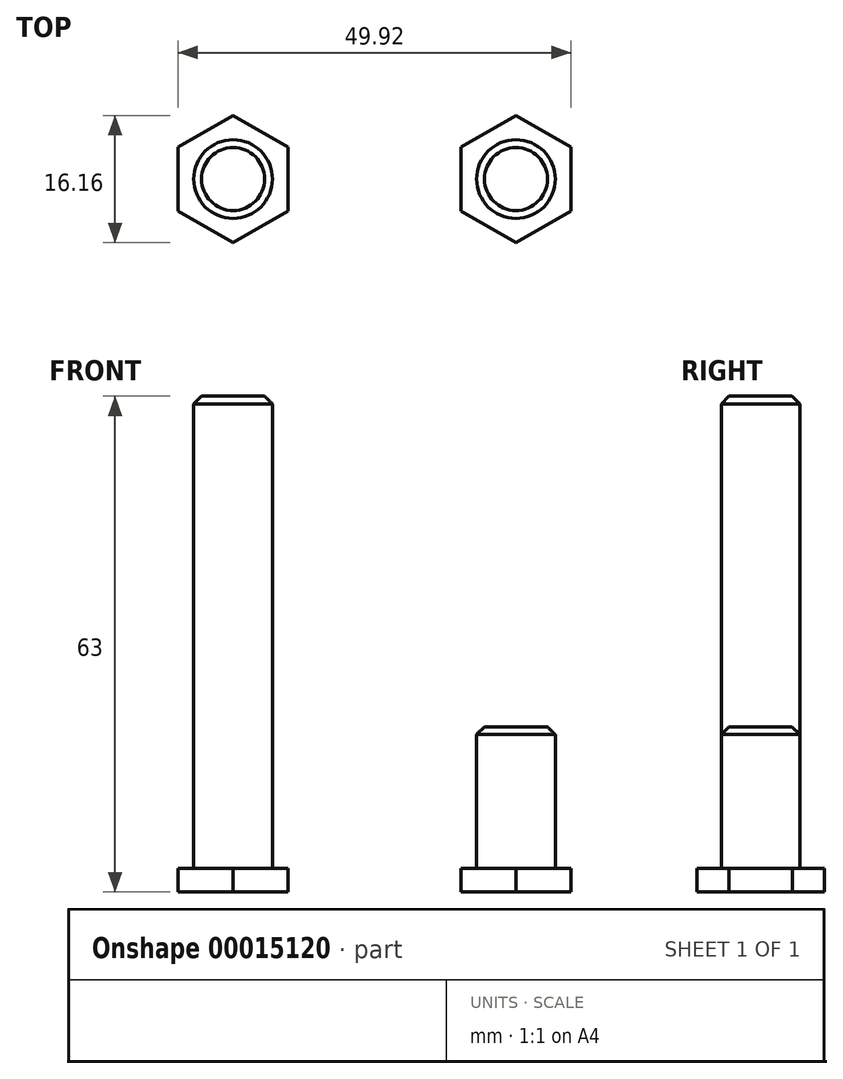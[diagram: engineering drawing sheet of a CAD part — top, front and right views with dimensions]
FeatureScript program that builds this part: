
annotation { "Feature Type Name" : "Feature", "Feature Type Description" : "" }
export const myFeature = defineFeature(function(context is Context, id is Id, definition is map)
    precondition{}
    {
        {
            var Q0;
            Q0=qCreatedBy(makeId("Top.planeOp"),FACE);
            var sketch = newSketch(context, id + "F0", { "sketchPlane" : qUnion([Q0])});
            skCircle(sketch, "E0.cCircle", {"center": v(17.96, 0) * mm, "radius": 7 * mm, "construction": true});
            skLineSegment(sketch, "E0.0", {"start": v(24.96, -4.04) * mm, "end": v(17.96, -8.08) * mm});
            skLineSegment(sketch, "E0.1", {"start": v(17.96, -8.08) * mm, "end": v(10.96, -4.04) * mm});
            skLineSegment(sketch, "E0.2", {"start": v(10.96, -4.04) * mm, "end": v(10.96, 4.04) * mm});
            skLineSegment(sketch, "E0.3", {"start": v(10.96, 4.04) * mm, "end": v(17.96, 8.08) * mm});
            skLineSegment(sketch, "E0.4", {"start": v(17.96, 8.08) * mm, "end": v(24.96, 4.04) * mm});
            skLineSegment(sketch, "E0.5", {"start": v(24.96, 4.04) * mm, "end": v(24.96, -4.04) * mm});
            skPoint(sketch, "E0.0.midPoint", {"position": v(21.46, -6.06) * mm});
            skLineSegment(sketch, "E1", {"start": v(0, 0) * mm, "end": v(0, 16.6) * mm, "construction": true});
            skLineSegment(sketch, "E2.0.MirrorCS", {"start": v(-10.96, -4.04) * mm, "end": v(-10.96, 4.04) * mm});
            skLineSegment(sketch, "E3.0.MirrorCS", {"start": v(-10.96, 4.04) * mm, "end": v(-17.96, 8.08) * mm});
            skLineSegment(sketch, "E4.0.MirrorCS", {"start": v(-17.96, 8.08) * mm, "end": v(-24.96, 4.04) * mm});
            skLineSegment(sketch, "E5.0.MirrorCS", {"start": v(-24.96, 4.04) * mm, "end": v(-24.96, -4.04) * mm});
            skPoint(sketch, "E6.0.MirrorP", {"position": v(-21.46, -6.06) * mm});
            skLineSegment(sketch, "E7.0.MirrorCS", {"start": v(-17.96, -8.08) * mm, "end": v(-10.96, -4.04) * mm});
            skLineSegment(sketch, "E8.0.MirrorCS", {"start": v(-24.96, -4.04) * mm, "end": v(-17.96, -8.08) * mm});
            skSolve(sketch);
        }
        {
            var Q0;
            Q0=makeQuery(id+"F0.imprint","IMPRINT",FACE,{"disambiguationData":[TD([[makeQuery(id+"F0.imprint","IMPRINT",EDGE,{"derivedFrom":sQuery(id+"F0.wireOp",EDGE,"E2.0.MirrorCS")}),1.0]])]});
            var Q1;
            Q1=makeQuery(id+"F0.imprint","IMPRINT",FACE,{"disambiguationData":[TD([[makeQuery(id+"F0.imprint","IMPRINT",EDGE,{"derivedFrom":sQuery(id+"F0.wireOp",EDGE,"E0.0")}),-1.0]])]});
            extrude(context, id + "F1", {"entities" : qUnion([Q0, Q1]), "depth" : 3 * mm});
        }
        {
            var Q0;
            Q0=makeQuery(id+"F1.opExtrude","CAP_FACE",FACE,{"disambiguationData":[OSD([sQuery(id+"F0.wireOp",EDGE,"E2.0.MirrorCS"),sQuery(id+"F0.wireOp",EDGE,"E3.0.MirrorCS"),sQuery(id+"F0.wireOp",EDGE,"E4.0.MirrorCS"),sQuery(id+"F0.wireOp",EDGE,"E5.0.MirrorCS"),sQuery(id+"F0.wireOp",EDGE,"E7.0.MirrorCS"),sQuery(id+"F0.wireOp",EDGE,"E8.0.MirrorCS")])],"isStart":false});
            var sketch = newSketch(context, id + "F2", { "sketchPlane" : qUnion([Q0])});
            skLineSegment(sketch, "E9.0.0", {"start": v(-17.96, -8.08) * mm, "end": v(-10.96, -4.04) * mm});
            skLineSegment(sketch, "E9.0.1", {"start": v(-10.96, -4.04) * mm, "end": v(-10.96, 4.04) * mm});
            skLineSegment(sketch, "E9.0.2", {"start": v(-10.96, 4.04) * mm, "end": v(-17.96, 8.08) * mm});
            skLineSegment(sketch, "E9.0.3", {"start": v(-17.96, 8.08) * mm, "end": v(-24.96, 4.04) * mm});
            skLineSegment(sketch, "E9.0.4", {"start": v(-24.96, 4.04) * mm, "end": v(-24.96, -4.04) * mm});
            skLineSegment(sketch, "E9.0.5", {"start": v(-24.96, -4.04) * mm, "end": v(-17.96, -8.08) * mm});
            skLineSegment(sketch, "E10.0.0", {"start": v(17.96, -8.08) * mm, "end": v(24.96, -4.04) * mm});
            skLineSegment(sketch, "E10.0.1", {"start": v(24.96, -4.04) * mm, "end": v(24.96, 4.04) * mm});
            skLineSegment(sketch, "E10.0.2", {"start": v(24.96, 4.04) * mm, "end": v(17.96, 8.08) * mm});
            skLineSegment(sketch, "E10.0.3", {"start": v(17.96, 8.08) * mm, "end": v(10.96, 4.04) * mm});
            skLineSegment(sketch, "E10.0.4", {"start": v(10.96, 4.04) * mm, "end": v(10.96, -4.04) * mm});
            skLineSegment(sketch, "E10.0.5", {"start": v(10.96, -4.04) * mm, "end": v(17.96, -8.08) * mm});
            skLineSegment(sketch, "E11", {"start": v(-17.96, 8.08) * mm, "end": v(-17.96, -8.08) * mm, "construction": true});
            skLineSegment(sketch, "E12", {"start": v(-24.96, 4.04) * mm, "end": v(-10.96, -4.04) * mm, "construction": true});
            skLineSegment(sketch, "E13", {"start": v(10.96, 4.04) * mm, "end": v(24.96, -4.04) * mm, "construction": true});
            skLineSegment(sketch, "E14", {"start": v(17.96, 8.08) * mm, "end": v(17.96, -8.08) * mm, "construction": true});
            skCircle(sketch, "E15", {"center": v(-17.96, 0) * mm, "radius": 5 * mm});
            skCircle(sketch, "E16", {"center": v(17.96, 0) * mm, "radius": 5 * mm});
            skSolve(sketch);
        }
        {
            var Q0;
            Q0=makeQuery(id+"F2.imprint","IMPRINT",FACE,{"disambiguationData":[TD([[makeQuery(id+"F2.imprint","IMPRINT",EDGE,{"derivedFrom":sQuery(id+"F2.wireOp",EDGE,"E16")}),1.0]])]});
            extrude(context, id + "F3", {"entities" : qUnion([Q0]), "operationType" : NewBodyOperationType.ADD, "depth" : 18 * mm});
        }
        {
            var Q0;
            Q0=makeQuery(id+"F2.imprint","IMPRINT",FACE,{"disambiguationData":[TD([[makeQuery(id+"F2.imprint","IMPRINT",EDGE,{"derivedFrom":sQuery(id+"F2.wireOp",EDGE,"E15")}),1.0]])]});
            extrude(context, id + "F4", {"entities" : qUnion([Q0]), "operationType" : NewBodyOperationType.ADD, "depth" : 60 * mm});
        }
        {
            var Q0;
            Q0=makeQuery(id+"F4.opExtrude","CAP_EDGE",EDGE,{"disambiguationData":[OSD([sQuery(id+"F2.wireOp",EDGE,"E15")])],"isStart":false});
            var Q1;
            Q1=makeQuery(id+"F3.opExtrude","CAP_EDGE",EDGE,{"disambiguationData":[OSD([sQuery(id+"F2.wireOp",EDGE,"E16")])],"isStart":false});
            chamfer(context, id + "F5", {"entities" : qUnion([Q0, Q1]), "width" : 1 * mm, "tangentPropagation" : true});
        }
    });
